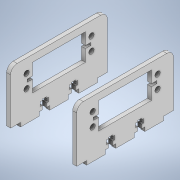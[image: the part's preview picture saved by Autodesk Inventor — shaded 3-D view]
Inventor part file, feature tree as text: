
AUTODESK INVENTOR PART (.ipt)
format: ipt  version: 2022 (Build 260153000, 153)  size: 356,864 bytes
history: native  units: mm
features: extrude x9, sketch x5, other x3, fillet x1, reference x1
ambient origin geometry x8: Origin, YZ Plane, XZ Plane, XY Plane, X Axis, Y Axis, Z Axis, Center Point
bodies: Solid1 (feature_tree)
feature tree (19):
  extrude  "Extrusion1"  Depth=39.8mm
  extrude  "Extrusion2"  Depth=3.0mm TaperAngle=0.0deg
  fillet  "Fillet1"  Radius=5.0mm
  extrude  "Extrusion4"  Depth=16.5mm
  extrude  "Extrusion5"  Depth=46.9mm
  extrude  "Extrusion6"  Depth=3.0mm TaperAngle=0.0deg
  extrude  "Extrusion7"  Depth=3.0mm TaperAngle=0.0deg
  extrude  "Extrusion8"  Depth=3.0mm TaperAngle=0.0deg
  extrude  "Extrusion9"  TaperAngle=0.0deg  [1 undecoded]
  extrude  "Extrusion10"  Depth=10.0mm TaperAngle=0.0deg
  reference  "Reference1"
  sketch  "Sketch4"  dims[d0=3.0mm d1=39.8mm]
  sketch  "Sketch6"  dims[d3=73.0mm d4=0.0mm]
  sketch  "Sketch7"  dims[d5=35.0mm d6=14.8mm d7=40.0mm d8=20.0mm d9=14.8mm d10=3.0mm d11=8.05mm d12=0.0mm d13=0.0mm d14=5.0mm]
  sketch  "Sketch9"  dims[d19=38.0mm d20=16.5mm]
  sketch  "Sketch10"  dims[d22=3.0mm d23=46.9mm d24=3.0mm d25=0.0mm d34=3.0mm d35=0.0mm d43=3.0mm d44=0.0mm d64=0.0mm d65=0.0mm d66=10.0mm d67=0.0mm d68=3.0mm d69=0.0mm d70=3.0mm d71=0.0mm d78=3.0mm d79=14.0mm d80=8.0mm d81=14.0mm d82=8.0mm d83=14.0mm d84=7.5mm d85=7.5mm d89=3.0mm d92=3.1mm d96=1.5mm d98=2.45mm d99=2.45mm d100=3.1mm d101=3.0mm d102=1.5mm d104=1.5mm d107=1.5mm d108=1.0mm d109=3.1mm d110=1.0mm d111=3.0mm d112=3.0mm d113=6.1mm d114=6.1mm d116=3.0mm d117=3.0mm d118=10.0mm d119=3.0mm d127=4.0mm d128=4.0mm d130=4.0mm d131=4.0mm d134=5.0mm d135=5.0mm d136=10.0mm d137=10.0mm d138=5.0mm d139=5.0mm d140=49.0mm d141=49.0mm d142=9.0mm d143=4.0mm d144=2.0mm d145=9.0mm d146=4.0mm d147=14.0mm d148=14.0mm d149=14.0mm d150=39.8mm d72=0.5mm d73=0.872665mm d74=0.5mm d75=0.872665mm]
  other  "<userpath>\rob.iam"
  other  "rob.iam"
  other  "Base4:1"
note: 1 required parameter value undecoded (feature->parameter linkage not recoverable at this tier; creation-order binding heuristic only, values carry confidence <= 0.55)
